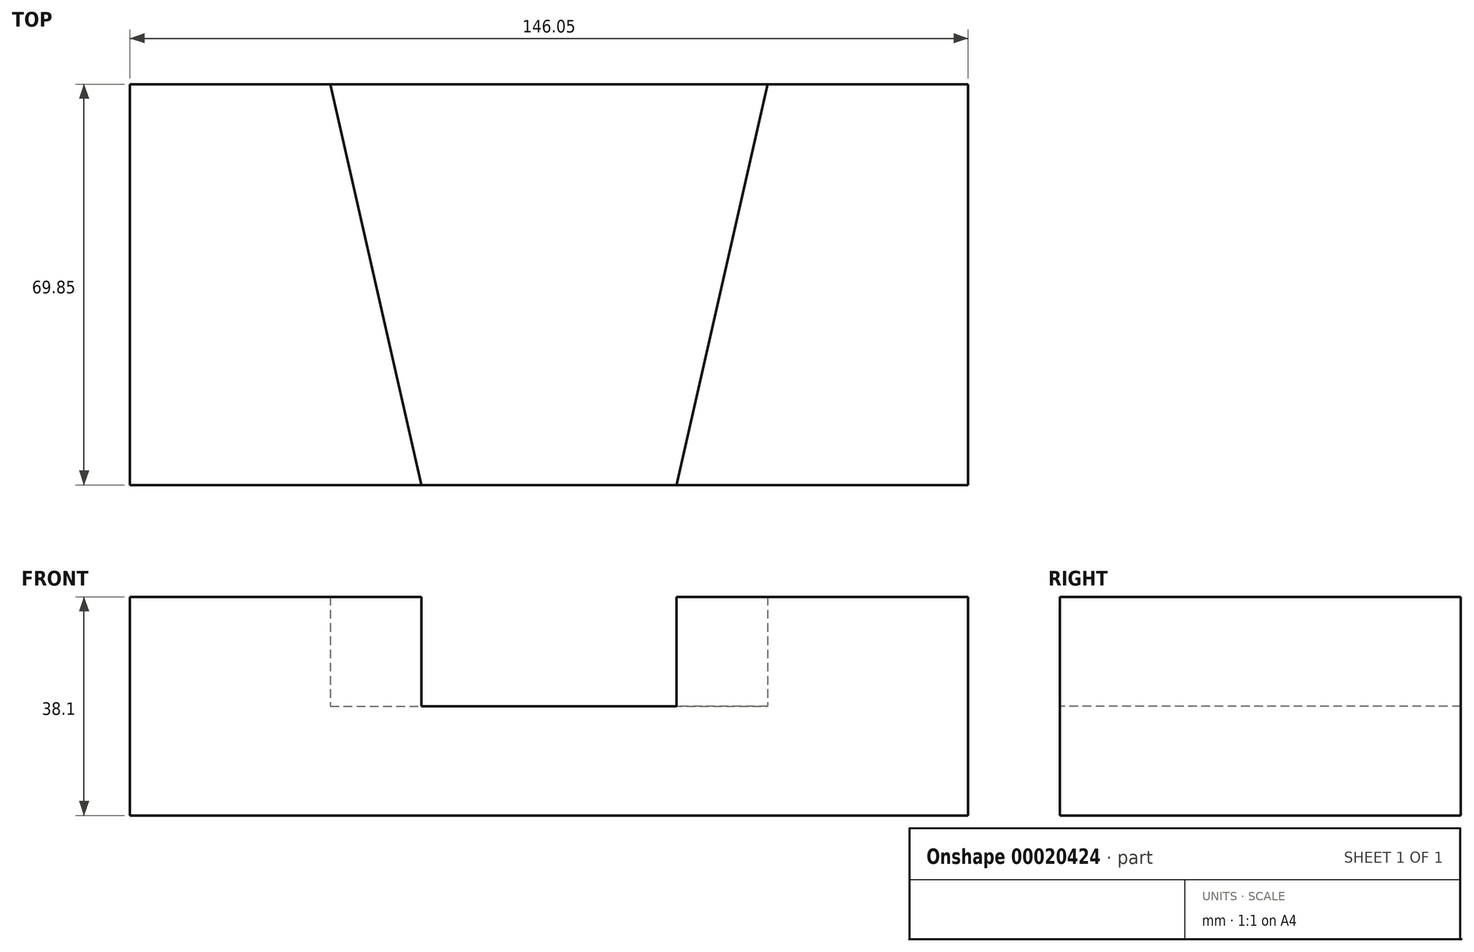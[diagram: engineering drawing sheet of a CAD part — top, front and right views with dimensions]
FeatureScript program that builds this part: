
annotation { "Feature Type Name" : "Feature", "Feature Type Description" : "" }
export const myFeature = defineFeature(function(context is Context, id is Id, definition is map)
    precondition{}
    {
        {
            var Q0;
            Q0=qCreatedBy(makeId("Top.planeOp"),FACE);
            var sketch = newSketch(context, id + "F0", { "sketchPlane" : qUnion([Q0])});
            skLineSegment(sketch, "E0.bottom", {"start": v(-72.66, 16.64) * mm, "end": v(73.39, 16.64) * mm});
            skLineSegment(sketch, "E0.top", {"start": v(-72.66, -53.21) * mm, "end": v(73.39, -53.21) * mm});
            skLineSegment(sketch, "E0.left", {"start": v(-72.66, 16.64) * mm, "end": v(-72.66, -53.21) * mm});
            skLineSegment(sketch, "E0.right", {"start": v(73.39, 16.64) * mm, "end": v(73.39, -53.21) * mm});
            skLineSegment(sketch, "E1", {"start": v(-37.74, 16.64) * mm, "end": v(-21.86, -53.21) * mm});
            skLineSegment(sketch, "E2", {"start": v(38.46, 16.64) * mm, "end": v(22.59, -53.21) * mm});
            skSolve(sketch);
        }
        {
            var Q0;
            {var subQ1=sQuery(id+"F0.wireOp",EDGE,"E0.left");Q0=makeQuery(id+"F0.imprint","IMPRINT",FACE,{"disambiguationData":[TD([[makeQuery(id+"F0.imprint","IMPRINT",EDGE,{"derivedFrom":subQ1}),1.0]])]});}
            extrude(context, id + "F1", {"entities" : qUnion([Q0]), "depth" : 38.1 * mm});
        }
        {
            var Q0;
            {var subQ1=sQuery(id+"F0.wireOp",EDGE,"E1");Q0=makeQuery(id+"F0.imprint","IMPRINT",FACE,{"disambiguationData":[TD([[makeQuery(id+"F0.imprint","IMPRINT",EDGE,{"derivedFrom":subQ1}),1.0]])]});}
            extrude(context, id + "F2", {"entities" : qUnion([Q0]), "operationType" : NewBodyOperationType.ADD, "depth" : 19.05 * mm});
        }
        {
            var Q0;
            {var subQ1=sQuery(id+"F0.wireOp",EDGE,"E0.right");Q0=makeQuery(id+"F0.imprint","IMPRINT",FACE,{"disambiguationData":[TD([[makeQuery(id+"F0.imprint","IMPRINT",EDGE,{"derivedFrom":subQ1}),-1.0]])]});}
            extrude(context, id + "F3", {"entities" : qUnion([Q0]), "operationType" : NewBodyOperationType.ADD, "depth" : 38.1 * mm});
        }
    });
